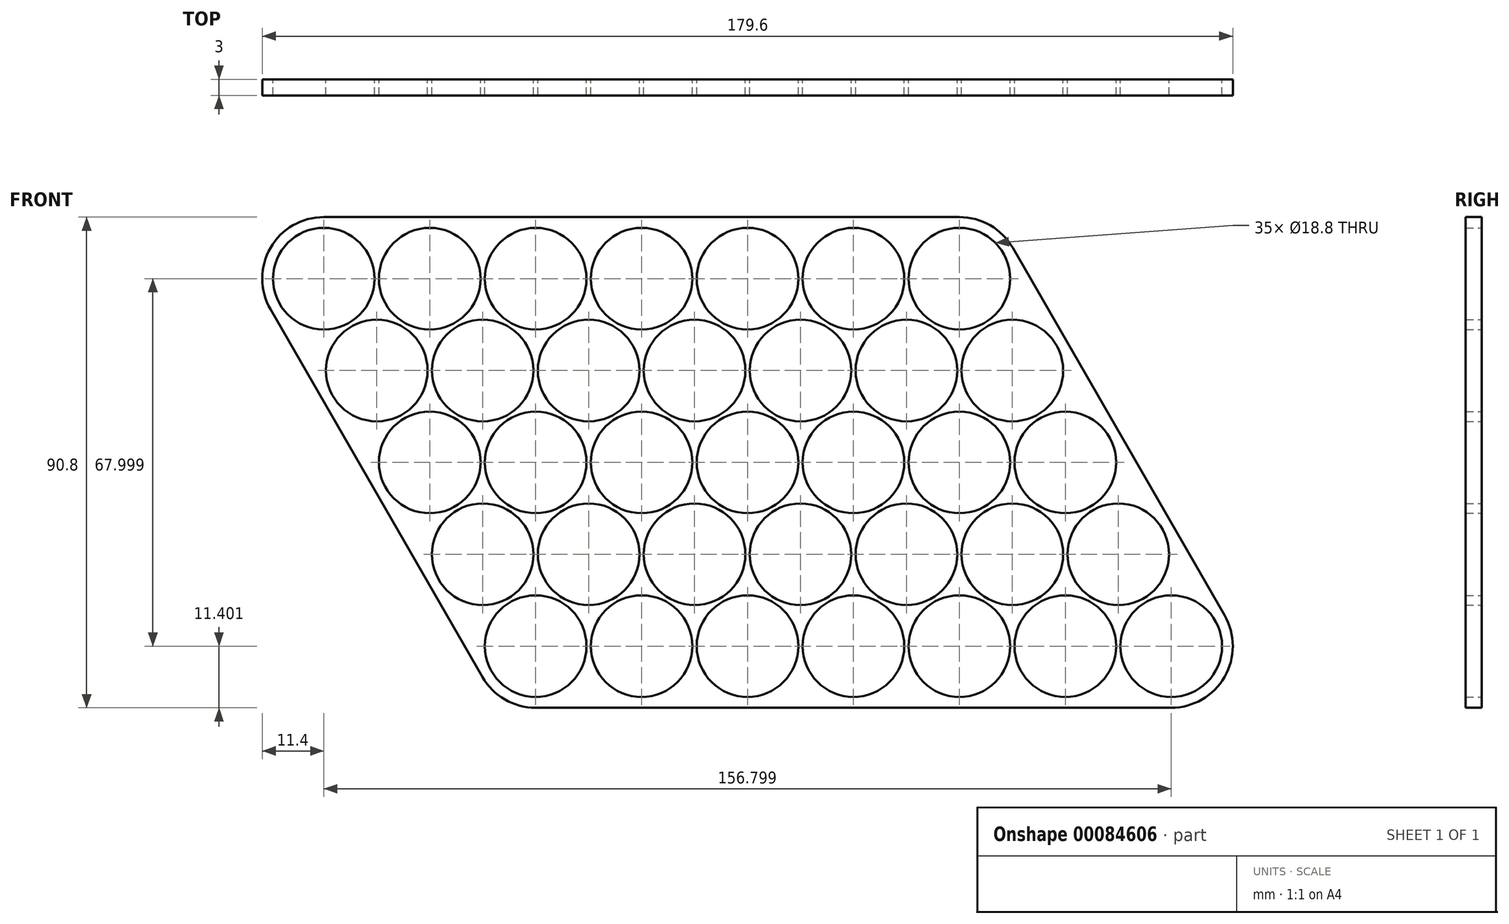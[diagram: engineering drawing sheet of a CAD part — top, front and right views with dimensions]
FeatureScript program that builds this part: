
annotation { "Feature Type Name" : "Feature", "Feature Type Description" : "" }
export const myFeature = defineFeature(function(context is Context, id is Id, definition is map)
    precondition{}
    {
        {
            var Q0;
            Q0=qCreatedBy(makeId("Front.planeOp"),FACE);
            var sketch = newSketch(context, id + "F0", { "sketchPlane" : qUnion([Q0]) });
            skCircle(sketch, "E0", {"center": v(0, 0) * mm, "radius": 9.4 * mm});
            skCircle(sketch, "E1.1.0.0", {"center": v(19.6, 0) * mm, "radius": 9.4 * mm});
            skCircle(sketch, "E1.2.0.0", {"center": v(39.2, 0) * mm, "radius": 9.4 * mm});
            skCircle(sketch, "E1.3.0.0", {"center": v(58.8, 0) * mm, "radius": 9.4 * mm});
            skLineSegment(sketch, "E1.direction1", {"start": v(0, 0) * mm, "end": v(19.6, 0) * mm, "construction": true});
            skLineSegment(sketch, "E2", {"start": v(0, -17) * mm, "end": v(73.2, -17) * mm, "construction": true});
            skLineSegment(sketch, "E3", {"start": v(9.8, 0) * mm, "end": v(9.8, -17) * mm, "construction": true});
            skCircle(sketch, "E4", {"center": v(9.8, -17) * mm, "radius": 9.4 * mm});
            skCircle(sketch, "E5.1.0.0", {"center": v(29.4, -17) * mm, "radius": 9.4 * mm});
            skCircle(sketch, "E5.2.0.0", {"center": v(49, -17) * mm, "radius": 9.4 * mm});
            skCircle(sketch, "E5.3.0.0", {"center": v(68.6, -17) * mm, "radius": 9.4 * mm});
            skLineSegment(sketch, "E5.direction1", {"start": v(9.8, -17) * mm, "end": v(29.4, -17) * mm, "construction": true});
            skLineSegment(sketch, "E6", {"start": v(-8.14, -4.7) * mm, "end": v(1.66, -21.7) * mm});
            skLineSegment(sketch, "E7", {"start": v(0, 9.4) * mm, "end": v(58.8, 9.4) * mm});
            skLineSegment(sketch, "E8", {"start": v(9.8, -17) * mm, "end": v(9.8, -26.4) * mm, "construction": true});
            skLineSegment(sketch, "E9", {"start": v(68.6, -17) * mm, "end": v(68.6, -26.4) * mm, "construction": true});
            skArc(sketch, "E10", {"start": v(58.8, 9.4) * mm, "mid": v(63.5, 8.14) * mm, "end": v(66.94, 4.7) * mm});
            skArc(sketch, "E11", {"start": v(76.74, -12.3) * mm, "mid": v(76.74, -21.7) * mm, "end": v(68.6, -26.4) * mm});
            skArc(sketch, "E12", {"start": v(9.8, -26.4) * mm, "mid": v(5.1, -25.14) * mm, "end": v(1.66, -21.7) * mm});
            skArc(sketch, "E13", {"start": v(-8.14, -4.7) * mm, "mid": v(-8.14, 4.7) * mm, "end": v(0, 9.4) * mm});
            skArc(sketch, "E14.0", {"start": v(0, 11.4) * mm, "mid": v(-9.87, 5.7) * mm, "end": v(-9.88, -5.7) * mm});
            skLineSegment(sketch, "E15.0", {"start": v(0, 11.4) * mm, "end": v(58.8, 11.4) * mm});
            skLineSegment(sketch, "E16.0", {"start": v(-9.88, -5.7) * mm, "end": v(-0.08, -22.7) * mm});
            skArc(sketch, "E17.trimOffspring", {"start": v(9.8, -5.82) * mm, "mid": v(9.87, -5.71) * mm, "end": v(9.93, -5.6) * mm});
            skArc(sketch, "E18.trimOffspring", {"start": v(9.93, -5.6) * mm, "mid": v(9.86, -5.6) * mm, "end": v(9.8, -5.6) * mm});
            skCircle(sketch, "E19.0.4.0", {"center": v(78.4, 0) * mm, "radius": 9.4 * mm});
            skCircle(sketch, "E19.0.5.0", {"center": v(98, 0) * mm, "radius": 9.4 * mm});
            skCircle(sketch, "E20.0.4.0", {"center": v(88.2, -17) * mm, "radius": 9.4 * mm});
            skCircle(sketch, "E20.0.5.0", {"center": v(107.8, -17) * mm, "radius": 9.4 * mm});
            skLineSegment(sketch, "E21", {"start": v(58.8, 11.4) * mm, "end": v(98, 11.4) * mm});
            skLineSegment(sketch, "E22", {"start": v(0, 0) * mm, "end": v(9.8, -17) * mm, "construction": true});
            skCircle(sketch, "E23.1.0.0", {"center": v(19.6, -34) * mm, "radius": 9.4 * mm});
            skCircle(sketch, "E23.2.0.0", {"center": v(29.4, -51) * mm, "radius": 9.4 * mm});
            skLineSegment(sketch, "E23.direction1", {"start": v(9.8, -17) * mm, "end": v(19.6, -34) * mm, "construction": true});
            skCircle(sketch, "E24.1.0.0", {"center": v(39.2, -34) * mm, "radius": 9.4 * mm});
            skCircle(sketch, "E24.1.0.1", {"center": v(49, -51) * mm, "radius": 9.4 * mm});
            skCircle(sketch, "E24.2.0.0", {"center": v(58.8, -34) * mm, "radius": 9.4 * mm});
            skCircle(sketch, "E24.2.0.1", {"center": v(68.6, -51) * mm, "radius": 9.4 * mm});
            skCircle(sketch, "E24.3.0.0", {"center": v(78.4, -34) * mm, "radius": 9.4 * mm});
            skCircle(sketch, "E24.3.0.1", {"center": v(88.2, -51) * mm, "radius": 9.4 * mm});
            skCircle(sketch, "E24.4.0.0", {"center": v(98, -34) * mm, "radius": 9.4 * mm});
            skCircle(sketch, "E24.4.0.1", {"center": v(107.8, -51) * mm, "radius": 9.4 * mm});
            skCircle(sketch, "E24.5.0.0", {"center": v(117.6, -34) * mm, "radius": 9.4 * mm});
            skCircle(sketch, "E24.5.0.1", {"center": v(127.4, -51) * mm, "radius": 9.4 * mm});
            skLineSegment(sketch, "E24.direction1", {"start": v(19.6, -34) * mm, "end": v(39.2, -34) * mm, "construction": true});
            skLineSegment(sketch, "E25", {"start": v(-0.08, -22.7) * mm, "end": v(19.52, -56.7) * mm});
            skArc(sketch, "E26.0", {"start": v(29.27, -62.4) * mm, "mid": v(29.33, -62.4) * mm, "end": v(29.4, -62.4) * mm});
            skCircle(sketch, "E27.0.6.0", {"center": v(117.6, 0) * mm, "radius": 9.4 * mm});
            skCircle(sketch, "E28.0.6.0", {"center": v(127.4, -17) * mm, "radius": 9.4 * mm});
            skCircle(sketch, "E29.0.6.0", {"center": v(137.2, -34) * mm, "radius": 9.4 * mm});
            skCircle(sketch, "E29.2.6.0", {"center": v(147, -51) * mm, "radius": 9.4 * mm});
            skLineSegment(sketch, "E30", {"start": v(98, 11.4) * mm, "end": v(117.6, 11.4) * mm});
            skCircle(sketch, "E31.0.3.0", {"center": v(39.2, -68) * mm, "radius": 9.4 * mm});
            skCircle(sketch, "E32.1.0.0", {"center": v(58.8, -68) * mm, "radius": 9.4 * mm});
            skCircle(sketch, "E32.2.0.0", {"center": v(78.4, -68) * mm, "radius": 9.4 * mm});
            skCircle(sketch, "E32.3.0.0", {"center": v(98, -68) * mm, "radius": 9.4 * mm});
            skCircle(sketch, "E32.4.0.0", {"center": v(117.6, -68) * mm, "radius": 9.4 * mm});
            skCircle(sketch, "E32.5.0.0", {"center": v(137.2, -68) * mm, "radius": 9.4 * mm});
            skCircle(sketch, "E32.6.0.0", {"center": v(156.8, -68) * mm, "radius": 9.4 * mm});
            skLineSegment(sketch, "E32.direction1", {"start": v(39.2, -68) * mm, "end": v(58.8, -68) * mm, "construction": true});
            skArc(sketch, "E33.0", {"start": v(29.32, -73.7) * mm, "mid": v(33.5, -77.87) * mm, "end": v(39.2, -79.4) * mm});
            skLineSegment(sketch, "E34", {"start": v(19.52, -56.7) * mm, "end": v(29.32, -73.7) * mm});
            skLineSegment(sketch, "E35", {"start": v(39.2, -79.4) * mm, "end": v(156.8, -79.4) * mm});
            skArc(sketch, "E36", {"start": v(127.48, 5.7) * mm, "mid": v(123.3, 9.87) * mm, "end": v(117.6, 11.4) * mm});
            skArc(sketch, "E37", {"start": v(156.8, -79.4) * mm, "mid": v(166.67, -73.7) * mm, "end": v(166.68, -62.3) * mm});
            skLineSegment(sketch, "E38", {"start": v(127.48, 5.7) * mm, "end": v(166.68, -62.3) * mm});
            skSolve(sketch);
        }
        {
            var Q0;
            Q0=qSketchRegion(id+"F0",true);
            var Q1;
            {var subQ3=sQuery(id+"F0.wireOp",EDGE,"E1.1.0.0");Q1=makeQuery(id+"F0.imprint","IMPRINT",FACE,{"disambiguationData":[TD([[makeQuery(id+"F0.imprint","IMPRINT",EDGE,{"derivedFrom":subQ3}),-1.0]])]});}
            extrude(context, id + "F1", {"entities" : qUnion([Q0, Q1]), "depth" : 3 * mm});
        }
    });
